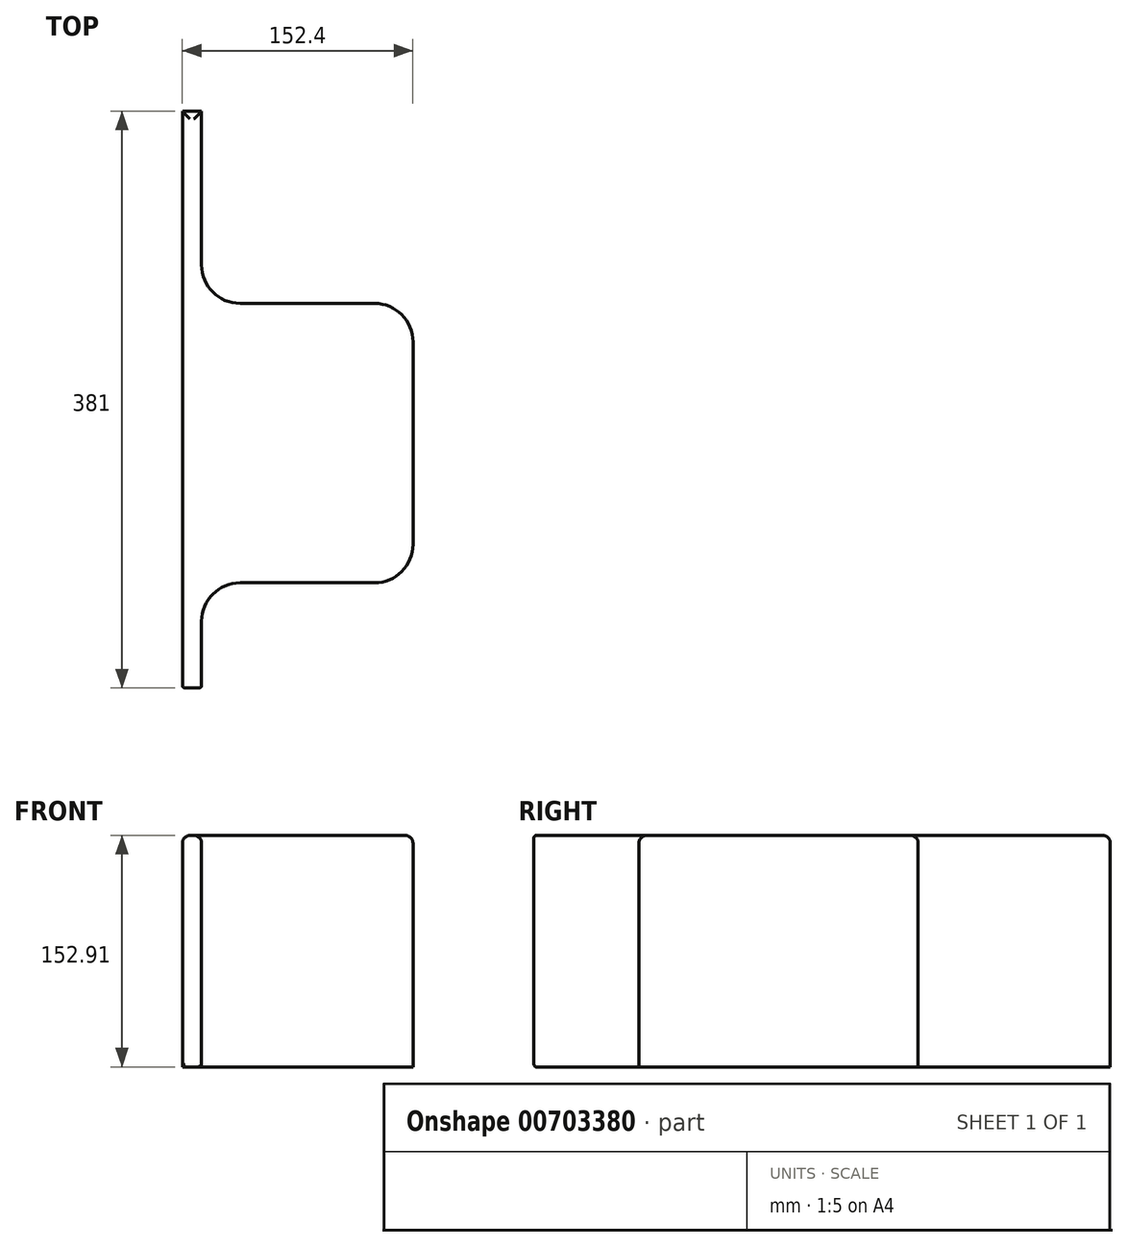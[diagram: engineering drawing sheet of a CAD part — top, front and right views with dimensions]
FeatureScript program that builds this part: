
annotation { "Feature Type Name" : "Feature", "Feature Type Description" : "" }
export const myFeature = defineFeature(function(context is Context, id is Id, definition is map)
    precondition{}
    {
        {
            var Q0;
            Q0=qCreatedBy(makeId("Top.planeOp"),FACE);
            var sketch = newSketch(context, id + "F0", { "sketchPlane" : qUnion([Q0])});
            skLineSegment(sketch, "E0.bottom", {"start": v(-136.12, -93.27) * mm, "end": v(-148.82, -93.27) * mm});
            skLineSegment(sketch, "E0.top", {"start": v(-136.12, 287.73) * mm, "end": v(-148.82, 287.73) * mm});
            skLineSegment(sketch, "E0.left", {"start": v(-136.12, -93.27) * mm, "end": v(-136.12, -23.88) * mm});
            skLineSegment(sketch, "E0.right", {"start": v(-148.82, -93.27) * mm, "end": v(-148.82, 287.73) * mm});
            skLineSegment(sketch, "E1.bottom", {"start": v(-136.12, 160.73) * mm, "end": v(3.58, 160.73) * mm});
            skLineSegment(sketch, "E1.top", {"start": v(-136.12, -23.88) * mm, "end": v(3.58, -23.88) * mm});
            skLineSegment(sketch, "E1.right", {"start": v(3.58, 160.73) * mm, "end": v(3.58, -23.88) * mm});
            skLineSegment(sketch, "E2.trimOffspring", {"start": v(-136.12, 160.73) * mm, "end": v(-136.12, 287.73) * mm});
            skSolve(sketch);
        }
        {
            var Q0;
            Q0=makeQuery(id+"F0.imprint","IMPRINT",FACE,{"disambiguationData":[TD([[makeQuery(id+"F0.imprint","IMPRINT",EDGE,{"derivedFrom":sQuery(id+"F0.wireOp",EDGE,"E0.bottom")}),-1.0]])]});
            extrude(context, id + "F1", {"entities" : qUnion([Q0]), "depth" : 152.9 * mm, "offsetDistance" : 25.4 * mm});
        }
        {
            var Q0;
            Q0=makeQuery(id+"F1.opExtrude","SWEPT_EDGE",EDGE,{"disambiguationData":[OSD([sQuery(id+"F0.wireOp",EDGE,"E0.left"),sQuery(id+"F0.wireOp",EDGE,"E1.top")])]});
            var Q1;
            Q1=makeQuery(id+"F1.opExtrude","SWEPT_EDGE",EDGE,{"disambiguationData":[OSD([sQuery(id+"F0.wireOp",EDGE,"E1.top"),sQuery(id+"F0.wireOp",EDGE,"E1.right")])]});
            var Q2;
            Q2=makeQuery(id+"F1.opExtrude","SWEPT_EDGE",EDGE,{"disambiguationData":[OSD([sQuery(id+"F0.wireOp",EDGE,"E1.bottom"),sQuery(id+"F0.wireOp",EDGE,"E1.right")])]});
            var Q3;
            Q3=makeQuery(id+"F1.opExtrude","SWEPT_EDGE",EDGE,{"disambiguationData":[OSD([sQuery(id+"F0.wireOp",EDGE,"E1.bottom"),sQuery(id+"F0.wireOp",EDGE,"E2.trimOffspring")])]});
            fillet(context, id + "F2", {"entities" : qUnion([Q0, Q1, Q2, Q3]), "radius" : 25.4 * mm, "tangentPropagation" : true, "allowEdgeOverflow" : false});
        }
        {
            var Q0;
            Q0=makeQuery(id+"F1.opExtrude","SWEPT_FACE",FACE,{"disambiguationData":[OSD([sQuery(id+"F0.wireOp",EDGE,"E0.bottom")])]});
            fillet(context, id + "F3", {"entities" : qUnion([Q0]), "radius" : 1.59 * mm, "tangentPropagation" : true, "allowEdgeOverflow" : false});
        }
        {
            var Q0;
            Q0=makeQuery(id+"F1.opExtrude","CAP_FACE",FACE,{"disambiguationData":[OSD([sQuery(id+"F0.wireOp",EDGE,"E0.bottom"),sQuery(id+"F0.wireOp",EDGE,"E0.top"),sQuery(id+"F0.wireOp",EDGE,"E0.left"),sQuery(id+"F0.wireOp",EDGE,"E0.right"),sQuery(id+"F0.wireOp",EDGE,"E1.bottom"),sQuery(id+"F0.wireOp",EDGE,"E1.top"),sQuery(id+"F0.wireOp",EDGE,"E1.right"),sQuery(id+"F0.wireOp",EDGE,"E2.trimOffspring")])],"isStart":false});
            fillet(context, id + "F4", {"entities" : qUnion([Q0]), "radius" : 5.08 * mm, "tangentPropagation" : true, "allowEdgeOverflow" : false});
        }
    });
